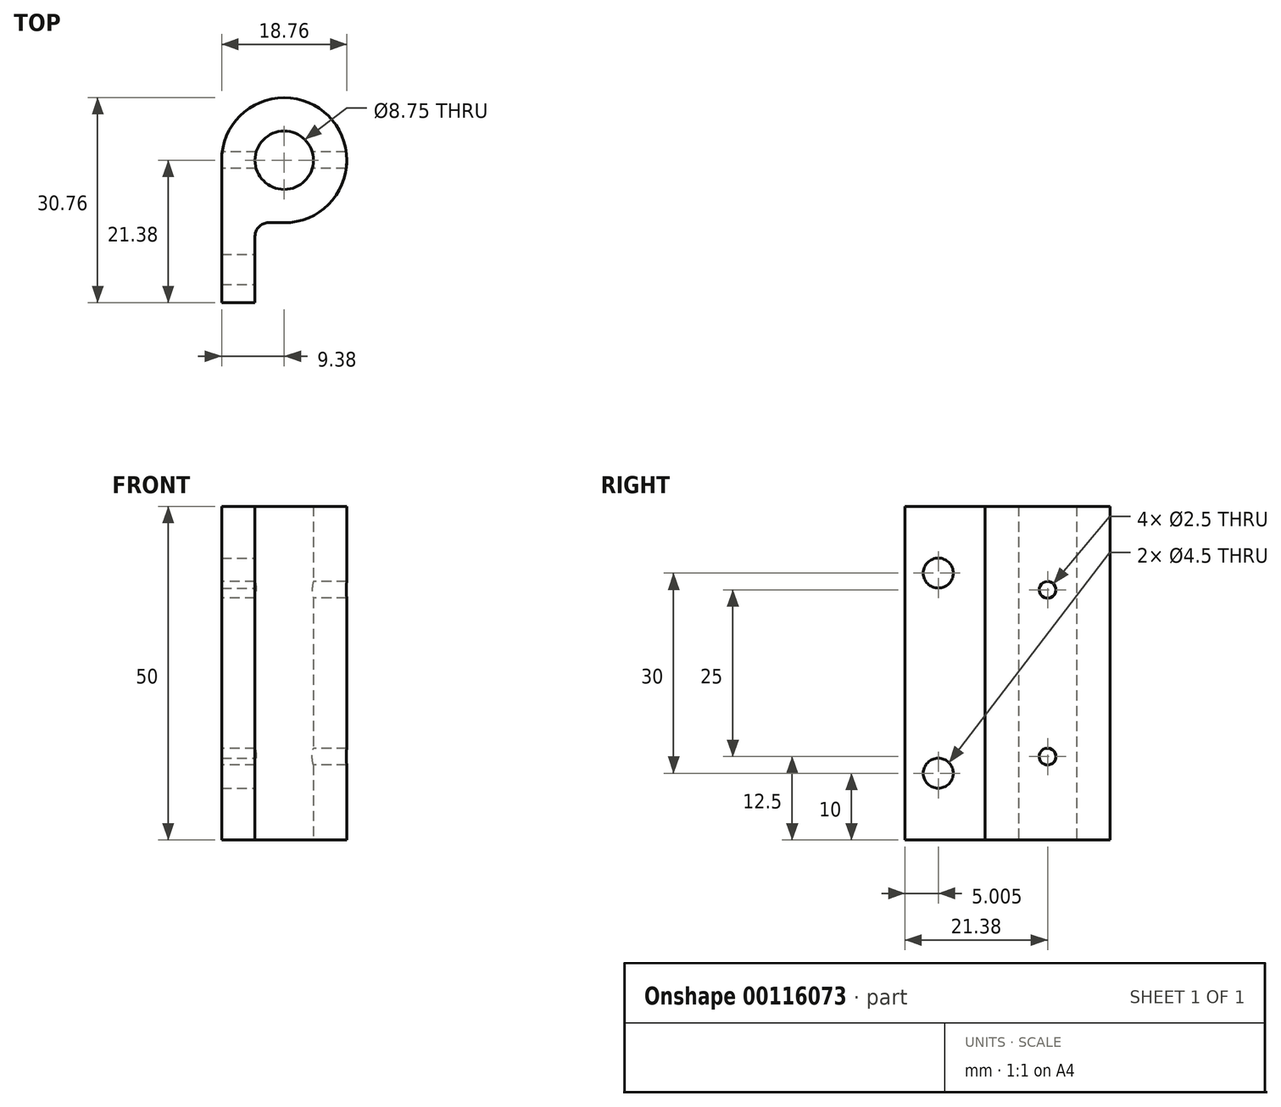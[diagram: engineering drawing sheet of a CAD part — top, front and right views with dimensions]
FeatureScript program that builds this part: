
annotation { "Feature Type Name" : "Feature", "Feature Type Description" : "" }
export const myFeature = defineFeature(function(context is Context, id is Id, definition is map)
    precondition{}
    {
        {
            var Q0;
            Q0=qCreatedBy(makeId("Top.planeOp"),FACE);
            var sketch = newSketch(context, id + "F0", { "sketchPlane" : qUnion([Q0])});
            skCircle(sketch, "E0", {"center": v(0, 0) * mm, "radius": 4.38 * mm});
            skArc(sketch, "E1", {"start": v(0, -9.38) * mm, "mid": v(6.63, 6.63) * mm, "end": v(-9.38, 0) * mm});
            skLineSegment(sketch, "E2", {"start": v(-9.38, 0) * mm, "end": v(-9.38, -21.38) * mm});
            skLineSegment(sketch, "E3", {"start": v(-9.37, -21.38) * mm, "end": v(-4.37, -21.38) * mm});
            skLineSegment(sketch, "E4", {"start": v(-4.38, -21.38) * mm, "end": v(-4.38, -11.38) * mm});
            skLineSegment(sketch, "E5", {"start": v(-2.37, -9.38) * mm, "end": v(0, -9.38) * mm});
            skPoint(sketch, "E6.orphan", {"position": v(0, -9.38) * mm});
            skPoint(sketch, "E7.visualSharp", {"position": v(-4.38, -9.38) * mm});
            skArc(sketch, "E7.filletArc", {"start": v(-2.37, -9.38) * mm, "mid": v(-3.79, -9.96) * mm, "end": v(-4.37, -11.38) * mm});
            skLineSegment(sketch, "E8", {"start": v(-4.37, -17.88) * mm, "end": v(-11.38, -17.88) * mm, "construction": true});
            skLineSegment(sketch, "E9.bottom", {"start": v(-4.37, -15.88) * mm, "end": v(-11.38, -15.88) * mm, "construction": true});
            skLineSegment(sketch, "E9.top", {"start": v(-4.37, -19.88) * mm, "end": v(-11.38, -19.88) * mm, "construction": true});
            skLineSegment(sketch, "E9.left", {"start": v(-4.38, -15.88) * mm, "end": v(-4.38, -19.88) * mm, "construction": true});
            skLineSegment(sketch, "E9.right", {"start": v(-11.38, -15.88) * mm, "end": v(-11.38, -19.88) * mm, "construction": true});
            skSolve(sketch);
        }
        {
            var Q0;
            Q0=makeQuery(id+"F0.imprint","IMPRINT",FACE,{"disambiguationData":[TD([[makeQuery(id+"F0.imprint","IMPRINT",EDGE,{"derivedFrom":sQuery(id+"F0.wireOp",EDGE,"E0")}),-1.0]])]});
            var Q1;
            {var subQ4=sQuery(id+"F0.wireOp",EDGE,"E3");Q1=makeQuery(id+"F0.imprint","IMPRINT",FACE,{"disambiguationData":[TD([[makeQuery(id+"F0.imprint","IMPRINT",EDGE,{"derivedFrom":subQ4}),1.0]])]});}
            var Q2;
            {var subQ1=sQuery(id+"F0.wireOp",EDGE,"E1");var subQ3=sQuery(id+"F0.wireOp",EDGE,"E2");var subQ4=makeQuery(id+"F0.imprint","INTERSECT",VERTEX,{"derivedFrom":[subQ1,subQ3]});Q2=makeQuery(id+"F0.imprint","IMPRINT",FACE,{"disambiguationData":[TD([[makeQuery(id+"F0.imprint","IMPRINT",EDGE,{"disambiguationData":[TD([[subQ4,-1.0]])],"derivedFrom":subQ3}),1.0]])]});}
            extrude(context, id + "F1", {"entities" : qUnion([Q0, Q1, Q2]), "depth" : 50 * mm});
        }
        {
            var Q0;
            Q0=qCreatedBy(makeId("Right.planeOp"),FACE);
            var sketch = newSketch(context, id + "F2", { "sketchPlane" : qUnion([Q0])});
            skCircle(sketch, "E10", {"center": v(0, 12.5) * mm, "radius": 1.25 * mm});
            skCircle(sketch, "E11", {"center": v(0, 37.5) * mm, "radius": 1.25 * mm});
            skSolve(sketch);
        }
        {
            var Q0;
            Q0 = qSketchRegion(id + "F2", true);
            extrude(context, id + "F3", {"entities" : qUnion([Q0]), "operationType" : NewBodyOperationType.REMOVE, "endBound" : BoundingType.SYMMETRIC, "depth" : 25 * mm});
        }
        {
            var Q0;
            Q0=makeQuery(id+"F1.opExtrude","SWEPT_FACE",FACE,{"disambiguationData":[OSD([sQuery(id+"F0.wireOp",EDGE,"E4")])]});
            var sketch = newSketch(context, id + "F4", { "sketchPlane" : qUnion([Q0])});
            skCircle(sketch, "E12", {"center": v(-16.38, 40) * mm, "radius": 4.5 * mm});
            skCircle(sketch, "E13", {"center": v(-16.38, 10) * mm, "radius": 4.5 * mm});
            skLineSegment(sketch, "E14", {"start": v(-16.38, 50) * mm, "end": v(-16.38, 0) * mm, "construction": true});
            skCircle(sketch, "E15", {"center": v(-16.38, 10) * mm, "radius": 2.25 * mm});
            skCircle(sketch, "E16", {"center": v(-16.38, 40) * mm, "radius": 2.25 * mm});
            skSolve(sketch);
        }
        {
            var Q0;
            Q0=makeQuery(id+"F4.imprint","IMPRINT",FACE,{"disambiguationData":[TD([[makeQuery(id+"F4.imprint","IMPRINT",EDGE,{"derivedFrom":sQuery(id+"F4.wireOp",EDGE,"E16")}),1.0]])]});
            var Q1;
            Q1=makeQuery(id+"F4.imprint","IMPRINT",FACE,{"disambiguationData":[TD([[makeQuery(id+"F4.imprint","IMPRINT",EDGE,{"derivedFrom":sQuery(id+"F4.wireOp",EDGE,"E15")}),1.0]])]});
            extrude(context, id + "F5", {"entities" : qUnion([Q0, Q1]), "operationType" : NewBodyOperationType.REMOVE, "endBound" : BoundingType.THROUGH_ALL, "oppositeDirection" : true, "depth" : 25 * mm});
        }
    });
